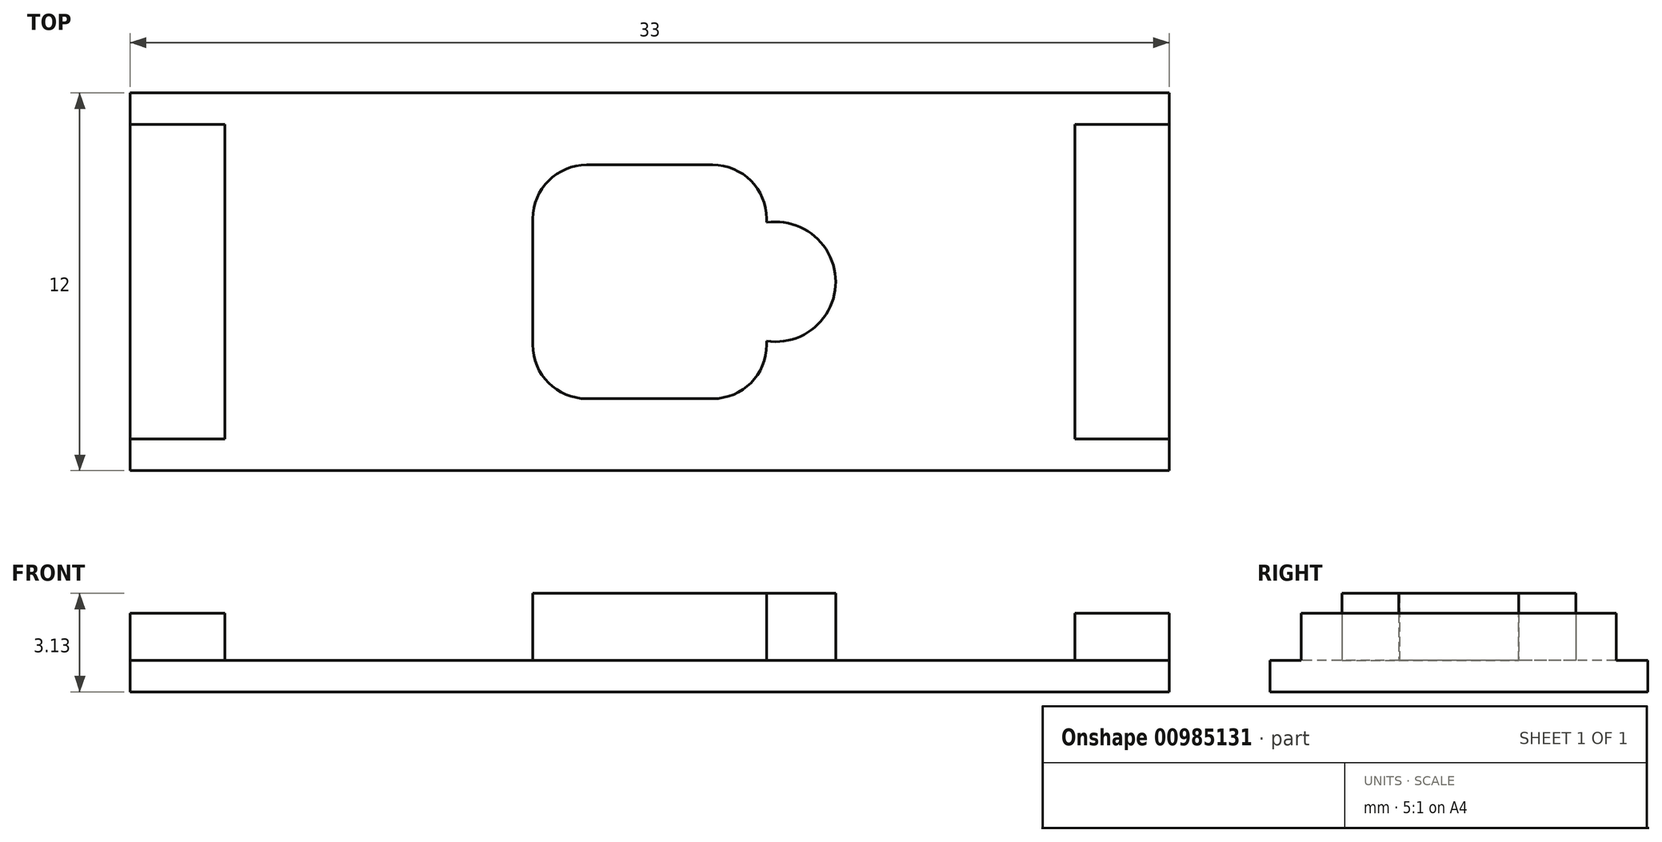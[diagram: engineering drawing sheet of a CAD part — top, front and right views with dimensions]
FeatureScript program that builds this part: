
annotation { "Feature Type Name" : "Feature", "Feature Type Description" : "" }
export const myFeature = defineFeature(function(context is Context, id is Id, definition is map)
    precondition{}
    {
        {
            assignVariable(context, id + "F0", {"name" : "led_thickness", "anyValue" : 2.13 * mm});
        }
        {
            assignVariable(context, id + "F1", {"name" : "led_strip_thickness", "anyValue" : 1 * mm});
        }
        {
            var Q0;
            Q0=qCreatedBy(makeId("Top.planeOp"),FACE);
            var sketch = newSketch(context, id + "F2", { "sketchPlane" : qUnion([Q0])});
            skLineSegment(sketch, "E0.bottom", {"start": v(2.5, 2.5) * mm, "end": v(-2.5, 2.5) * mm});
            skLineSegment(sketch, "E0.top", {"start": v(2.5, -2.5) * mm, "end": v(-2.5, -2.5) * mm});
            skLineSegment(sketch, "E0.left", {"start": v(2.5, 2.5) * mm, "end": v(2.5, -2.5) * mm});
            skLineSegment(sketch, "E0.right", {"start": v(-2.5, 2.5) * mm, "end": v(-2.5, -2.5) * mm});
            skPoint(sketch, "E0.middle", {"position": v(0, 0) * mm});
            skSolve(sketch);
        }
        {
            var Q0;
            Q0=makeQuery(id+"F2.imprint","IMPRINT",FACE,{"disambiguationData":[TD([[makeQuery(id+"F2.imprint","IMPRINT",EDGE,{"derivedFrom":sQuery(id+"F2.wireOp",EDGE,"E0.bottom")}),1.0]])]});
            var sketch = newSketch(context, id + "F3", { "sketchPlane" : qUnion([Q0])});
            skLineSegment(sketch, "E1.bottom", {"start": v(2.5, 3.75) * mm, "end": v(-2.5, 3.75) * mm});
            skLineSegment(sketch, "E1.top", {"start": v(2.5, -3.75) * mm, "end": v(-2.5, -3.75) * mm});
            skLineSegment(sketch, "E1.left", {"start": v(2.5, 3.75) * mm, "end": v(2.5, -3.75) * mm});
            skLineSegment(sketch, "E1.right", {"start": v(-2.5, 3.75) * mm, "end": v(-2.5, -3.75) * mm});
            skPoint(sketch, "E1.middle", {"position": v(0, 0) * mm});
            skLineSegment(sketch, "E2.bottom", {"start": v(4.5, 1.5) * mm, "end": v(3.5, 1.5) * mm, "construction": true});
            skLineSegment(sketch, "E2.top", {"start": v(4.5, -1.5) * mm, "end": v(3.5, -1.5) * mm, "construction": true});
            skLineSegment(sketch, "E2.left", {"start": v(4.5, 1.5) * mm, "end": v(4.5, -1.5) * mm, "construction": true});
            skLineSegment(sketch, "E2.right", {"start": v(3.5, 1.5) * mm, "end": v(3.5, -1.5) * mm, "construction": true});
            skPoint(sketch, "E2.middle", {"position": v(4, 0) * mm});
            skCircle(sketch, "E3", {"center": v(4, 0) * mm, "radius": 1.9 * mm});
            skSolve(sketch);
        }
        {
            var Q0;
            Q0 = qSketchRegion(id + "F2", true);
            extrude(context, id + "F4", {"entities" : qUnion([Q0]), "depth" : getVariable(context, 'led_thickness'), "offsetDistance" : 25 * mm});
        }
        {
            var Q0;
            {var subQ0=sQuery(id+"F3.wireOp",EDGE,"E3");var subQ1=sQuery(id+"F3.wireOp",EDGE,"E1.left");var subQ2=makeQuery(id+"F3.imprint","INTERSECT",VERTEX,{"disambiguationData":[OD(0.0)],"derivedFrom":[subQ1,subQ0]});Q0=makeQuery(id+"F3.imprint","IMPRINT",FACE,{"disambiguationData":[TD([[makeQuery(id+"F3.imprint","IMPRINT",EDGE,{"disambiguationData":[TD([[subQ2,-1.0]])],"derivedFrom":subQ1}),1.0]])]});}
            extrude(context, id + "F5", {"entities" : qUnion([Q0]), "depth" : getVariable(context, 'led_thickness'), "offsetDistance" : 25 * mm});
        }
        {
            var Q0;
            Q0=makeQuery(id+"F2.imprint","IMPRINT",FACE,{"disambiguationData":[TD([[makeQuery(id+"F2.imprint","IMPRINT",EDGE,{"derivedFrom":sQuery(id+"F2.wireOp",EDGE,"E0.bottom")}),1.0]])]});
            var sketch = newSketch(context, id + "F6", { "sketchPlane" : qUnion([Q0])});
            skLineSegment(sketch, "E4.bottom", {"start": v(-16.5, 6) * mm, "end": v(16.5, 6) * mm});
            skLineSegment(sketch, "E4.top", {"start": v(-16.5, -6) * mm, "end": v(16.5, -6) * mm});
            skLineSegment(sketch, "E4.left", {"start": v(-16.5, 6) * mm, "end": v(-16.5, -6) * mm});
            skLineSegment(sketch, "E4.right", {"start": v(16.5, 6) * mm, "end": v(16.5, -6) * mm});
            skPoint(sketch, "E4.middle", {"position": v(0, 0) * mm});
            skLineSegment(sketch, "E5", {"start": v(-16.5, 0) * mm, "end": v(16.5, 0) * mm, "construction": true});
            skLineSegment(sketch, "E6", {"start": v(0, 6) * mm, "end": v(0, -6) * mm, "construction": true});
            skSolve(sketch);
        }
        {
            var Q0;
            Q0 = qSketchRegion(id + "F6", true);
            extrude(context, id + "F7", {"entities" : qUnion([Q0]), "oppositeDirection" : true, "depth" : getVariable(context, 'led_strip_thickness'), "offsetDistance" : 25 * mm});
        }
        {
            var Q0;
            Q0=makeQuery(id+"F6.imprint","IMPRINT",FACE,{"disambiguationData":[TD([[makeQuery(id+"F6.imprint","IMPRINT",EDGE,{"derivedFrom":sQuery(id+"F6.wireOp",EDGE,"E4.bottom")}),-1.0]])]});
            var sketch = newSketch(context, id + "F8", { "sketchPlane" : qUnion([Q0])});
            skLineSegment(sketch, "E7.0", {"start": v(2, 2) * mm, "end": v(-2, 2) * mm, "construction": true});
            skLineSegment(sketch, "E7.1", {"start": v(2, 2) * mm, "end": v(2, -2) * mm, "construction": true});
            skLineSegment(sketch, "E7.2", {"start": v(2, -2) * mm, "end": v(-2, -2) * mm, "construction": true});
            skLineSegment(sketch, "E7.3", {"start": v(-2, 2) * mm, "end": v(-2, -2) * mm, "construction": true});
            skArc(sketch, "E8", {"start": v(-2, 3.71) * mm, "mid": v(-3.21, 3.21) * mm, "end": v(-3.71, 2) * mm});
            skArc(sketch, "E9", {"start": v(3.71, 2) * mm, "mid": v(3.21, 3.21) * mm, "end": v(2, 3.71) * mm});
            skArc(sketch, "E10", {"start": v(-3.71, -2) * mm, "mid": v(-3.21, -3.21) * mm, "end": v(-2, -3.71) * mm});
            skLineSegment(sketch, "E11", {"start": v(2, 3.71) * mm, "end": v(-2, 3.71) * mm});
            skLineSegment(sketch, "E12", {"start": v(-3.71, 2) * mm, "end": v(-3.71, -2) * mm});
            skLineSegment(sketch, "E13", {"start": v(-2, -3.71) * mm, "end": v(2, -3.71) * mm});
            skLineSegment(sketch, "E14", {"start": v(3.71, 2) * mm, "end": v(3.71, -2) * mm});
            skArc(sketch, "E15.trimOffspring", {"start": v(2, -3.71) * mm, "mid": v(3.21, -3.21) * mm, "end": v(3.71, -2) * mm});
            skSolve(sketch);
        }
        {
            var Q0;
            Q0 = qSketchRegion(id + "F8", true);
            var Q1;
            Q1=makeQuery(id+"F4.opExtrude","CAP_FACE",FACE,{"disambiguationData":[OSD([sQuery(id+"F2.wireOp",EDGE,"E0.bottom"),sQuery(id+"F2.wireOp",EDGE,"E0.top"),sQuery(id+"F2.wireOp",EDGE,"E0.left"),sQuery(id+"F2.wireOp",EDGE,"E0.right")])],"isStart":false});
            extrude(context, id + "F9", {"entities" : qUnion([Q0]), "operationType" : NewBodyOperationType.ADD, "endBound" : BoundingType.UP_TO_SURFACE, "depth" : 25 * mm, "endBoundEntityFace" : qUnion([Q1]), "offsetDistance" : 25 * mm});
        }
        {
            var Q0;
            Q0=makeQuery(id+"F6.imprint","IMPRINT",FACE,{"disambiguationData":[TD([[makeQuery(id+"F6.imprint","IMPRINT",EDGE,{"derivedFrom":sQuery(id+"F6.wireOp",EDGE,"E4.bottom")}),-1.0]])]});
            var sketch = newSketch(context, id + "F10", { "sketchPlane" : qUnion([Q0])});
            skLineSegment(sketch, "E16.bottom", {"start": v(-16.5, 5) * mm, "end": v(-13.5, 5) * mm});
            skLineSegment(sketch, "E16.top", {"start": v(-16.5, -5) * mm, "end": v(-13.5, -5) * mm});
            skLineSegment(sketch, "E16.left", {"start": v(-16.5, 5) * mm, "end": v(-16.5, -5) * mm});
            skLineSegment(sketch, "E16.right", {"start": v(-13.5, 5) * mm, "end": v(-13.5, -5) * mm});
            skLineSegment(sketch, "E17.MirrorCS", {"start": v(16.5, -5) * mm, "end": v(13.5, -5) * mm});
            skLineSegment(sketch, "E18.MirrorCS", {"start": v(16.5, 5) * mm, "end": v(16.5, -5) * mm});
            skLineSegment(sketch, "E19.MirrorCS", {"start": v(16.5, 5) * mm, "end": v(13.5, 5) * mm});
            skLineSegment(sketch, "E20.MirrorCS", {"start": v(13.5, 5) * mm, "end": v(13.5, -5) * mm});
            skSolve(sketch);
        }
        {
            var Q0;
            Q0 = qSketchRegion(id + "F10", true);
            extrude(context, id + "F11", {"entities" : qUnion([Q0]), "operationType" : NewBodyOperationType.ADD, "depth" : 1.5 * mm, "offsetDistance" : 25 * mm});
        }
    });
